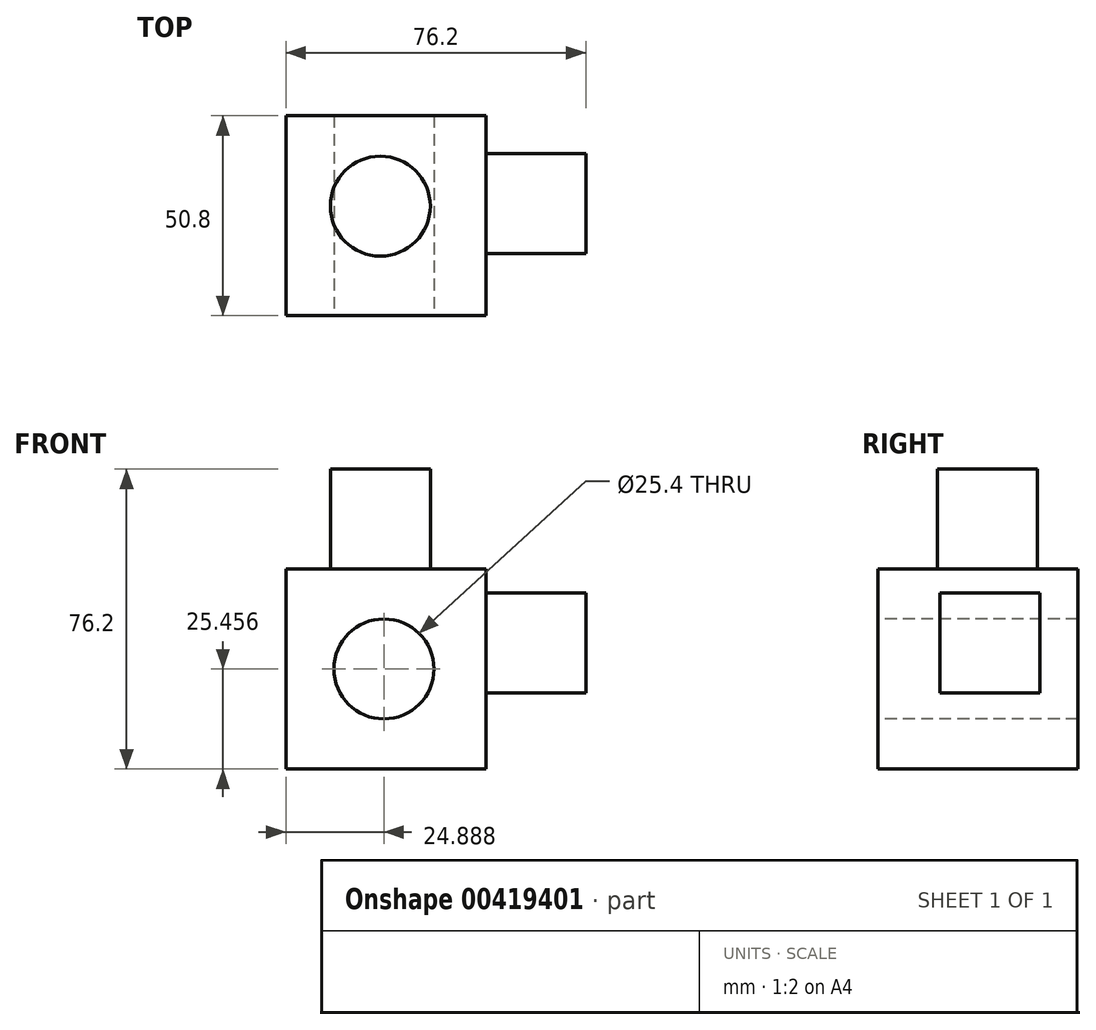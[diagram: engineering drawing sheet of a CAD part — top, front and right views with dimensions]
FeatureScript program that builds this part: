
annotation { "Feature Type Name" : "Feature", "Feature Type Description" : "" }
export const myFeature = defineFeature(function(context is Context, id is Id, definition is map)
    precondition{}
    {
        {
            var Q0;
            Q0=qCreatedBy(makeId("Front.planeOp"),FACE);
            var sketch = newSketch(context, id + "F0", { "sketchPlane" : qUnion([Q0])});
            skLineSegment(sketch, "E0", {"start": v(0, 0) * mm, "end": v(-50.8, 0) * mm});
            skLineSegment(sketch, "E1", {"start": v(-50.8, 0) * mm, "end": v(-50.8, 50.8) * mm});
            skLineSegment(sketch, "E2", {"start": v(-50.8, 50.8) * mm, "end": v(0, 50.8) * mm});
            skLineSegment(sketch, "E3", {"start": v(0, 50.8) * mm, "end": v(0, 0) * mm});
            skSolve(sketch);
        }
        {
            var Q0;
            Q0=makeQuery(id+"F0.imprint","IMPRINT",FACE,{"disambiguationData":[TD([[makeQuery(id+"F0.imprint","IMPRINT",EDGE,{"derivedFrom":sQuery(id+"F0.wireOp",EDGE,"E0")}),-1.0]])]});
            extrude(context, id + "F1", {"entities" : qUnion([Q0]), "depth" : 50.8 * mm});
        }
        {
            var Q0;
            Q0=makeQuery(id+"F1.opExtrude","CAP_FACE",FACE,{"disambiguationData":[OSD([sQuery(id+"F0.wireOp",EDGE,"E0"),sQuery(id+"F0.wireOp",EDGE,"E1"),sQuery(id+"F0.wireOp",EDGE,"E2"),sQuery(id+"F0.wireOp",EDGE,"E3")])],"isStart":false});
            var sketch = newSketch(context, id + "F2", { "sketchPlane" : qUnion([Q0])});
            skCircle(sketch, "E4", {"center": v(-25.91, 25.46) * mm, "radius": 12.7 * mm});
            skSolve(sketch);
        }
        {
            var Q0;
            Q0 = qSketchRegion(id + "F2", true);
            extrude(context, id + "F3", {"entities" : qUnion([Q0]), "operationType" : NewBodyOperationType.REMOVE, "oppositeDirection" : true, "depth" : 50.8 * mm});
        }
        {
            var Q0;
            Q0=makeQuery(id+"F1.opExtrude","SWEPT_FACE",FACE,{"disambiguationData":[OSD([sQuery(id+"F0.wireOp",EDGE,"E3")])]});
            var sketch = newSketch(context, id + "F4", { "sketchPlane" : qUnion([Q0])});
            skLineSegment(sketch, "E5.bottom", {"start": v(-9.6, 19.32) * mm, "end": v(-35, 19.32) * mm});
            skLineSegment(sketch, "E5.top", {"start": v(-9.6, 44.72) * mm, "end": v(-35, 44.72) * mm});
            skLineSegment(sketch, "E5.left", {"start": v(-9.6, 19.32) * mm, "end": v(-9.6, 44.72) * mm});
            skLineSegment(sketch, "E5.right", {"start": v(-35, 19.32) * mm, "end": v(-35, 44.72) * mm});
            skSolve(sketch);
        }
        {
            var Q0;
            Q0 = qSketchRegion(id + "F4", true);
            extrude(context, id + "F5", {"entities" : qUnion([Q0]), "operationType" : NewBodyOperationType.ADD, "depth" : 25.4 * mm});
        }
        {
            var Q0;
            Q0=makeQuery(id+"F1.opExtrude","SWEPT_FACE",FACE,{"disambiguationData":[OSD([sQuery(id+"F0.wireOp",EDGE,"E2")])]});
            var sketch = newSketch(context, id + "F6", { "sketchPlane" : qUnion([Q0])});
            skCircle(sketch, "E6", {"center": v(-26.82, -22.96) * mm, "radius": 12.7 * mm});
            skSolve(sketch);
        }
        {
            var Q0;
            Q0=makeQuery(id+"F6.imprint","IMPRINT",FACE,{"disambiguationData":[TD([[makeQuery(id+"F6.imprint","IMPRINT",EDGE,{"derivedFrom":sQuery(id+"F6.wireOp",EDGE,"E6")}),1.0]])]});
            extrude(context, id + "F7", {"entities" : qUnion([Q0]), "operationType" : NewBodyOperationType.ADD, "depth" : 25.4 * mm});
        }
    });
